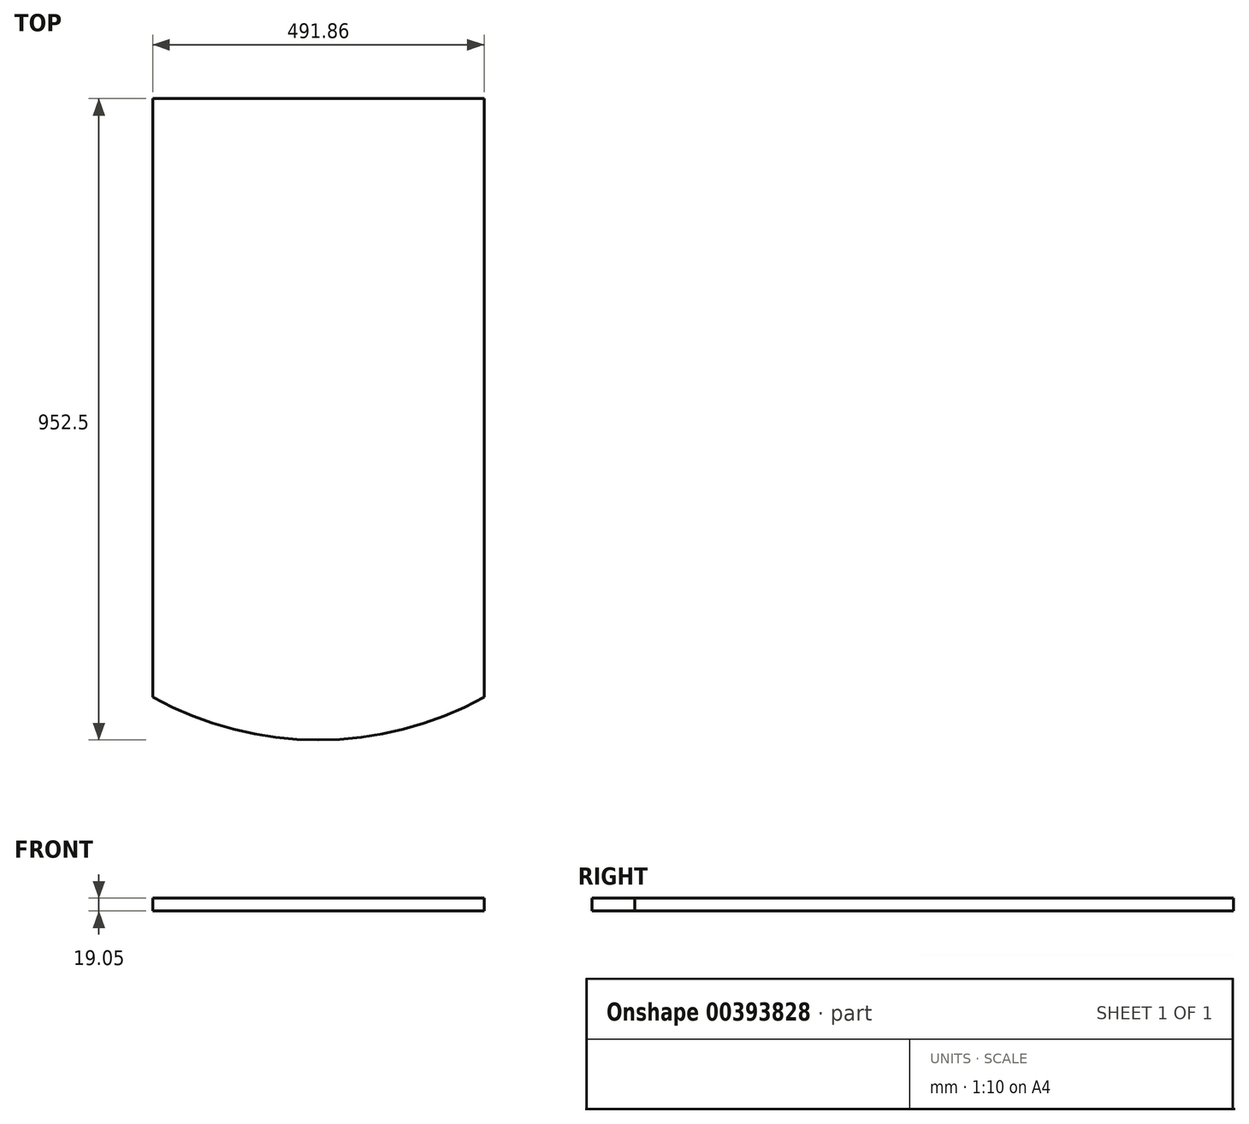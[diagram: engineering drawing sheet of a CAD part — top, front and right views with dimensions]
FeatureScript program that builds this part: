
annotation { "Feature Type Name" : "Feature", "Feature Type Description" : "" }
export const myFeature = defineFeature(function(context is Context, id is Id, definition is map)
    precondition{}
    {
        {
            var Q0;
            Q0=qCreatedBy(makeId("Top.planeOp"),FACE);
            var sketch = newSketch(context, id + "F0", { "sketchPlane" : qUnion([Q0])});
            skCircle(sketch, "E0", {"center": v(0, 0) * mm, "radius": 508 * mm});
            skLineSegment(sketch, "E1", {"start": v(245.93, 444.5) * mm, "end": v(245.93, -444.5) * mm});
            skLineSegment(sketch, "E2", {"start": v(-245.93, -444.5) * mm, "end": v(-245.93, 444.5) * mm});
            skLineSegment(sketch, "E3", {"start": v(245.93, 444.5) * mm, "end": v(-245.93, 444.5) * mm});
            skSolve(sketch);
        }
        {
            var Q0;
            {var subQ0=sQuery(id+"F0.wireOp",EDGE,"E1");Q0=makeQuery(id+"F0.imprint","IMPRINT",FACE,{"disambiguationData":[TD([[makeQuery(id+"F0.imprint","IMPRINT",EDGE,{"derivedFrom":subQ0}),-1.0]])]});}
            extrude(context, id + "F1", {"entities" : qUnion([Q0]), "depth" : 19.05 * mm});
        }
    });
